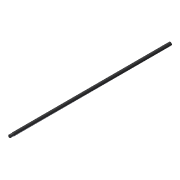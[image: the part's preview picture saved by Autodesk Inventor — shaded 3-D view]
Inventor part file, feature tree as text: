
AUTODESK INVENTOR PART (.ipt)
format: ipt  version: 2014 SP1 (Build 180222100, 222)  size: 76,288 bytes
history: native  units: in
note: dims shown in document units (in); Inventor stores cm internally (conversion verified against a paired STEP export)
features: extrude x2, sketch x2, thread x1
ambient origin geometry x8: Origin, YZ Plane, XZ Plane, XY Plane, X Axis, Y Axis, Z Axis, Center Point
bodies: Solid1 (feature_tree)
feature tree (5):
  extrude  "Extrusion1"  Depth=0.857in
  extrude  "Extrusion2"  Depth=1.0in TaperAngle=0.0deg
  thread  "Thread2"  [1 undecoded]
  sketch  "Sketch1"  dims[d0=0.584in d1=0.857in]
  sketch  "Sketch2"  dims[d2=44.422in d3=0.0in d4=1.0in d5=0.0in d11=1.0in d12=0.0in]
note: 1 required parameter value undecoded (feature->parameter linkage not recoverable at this tier; creation-order binding heuristic only, values carry confidence <= 0.55)
